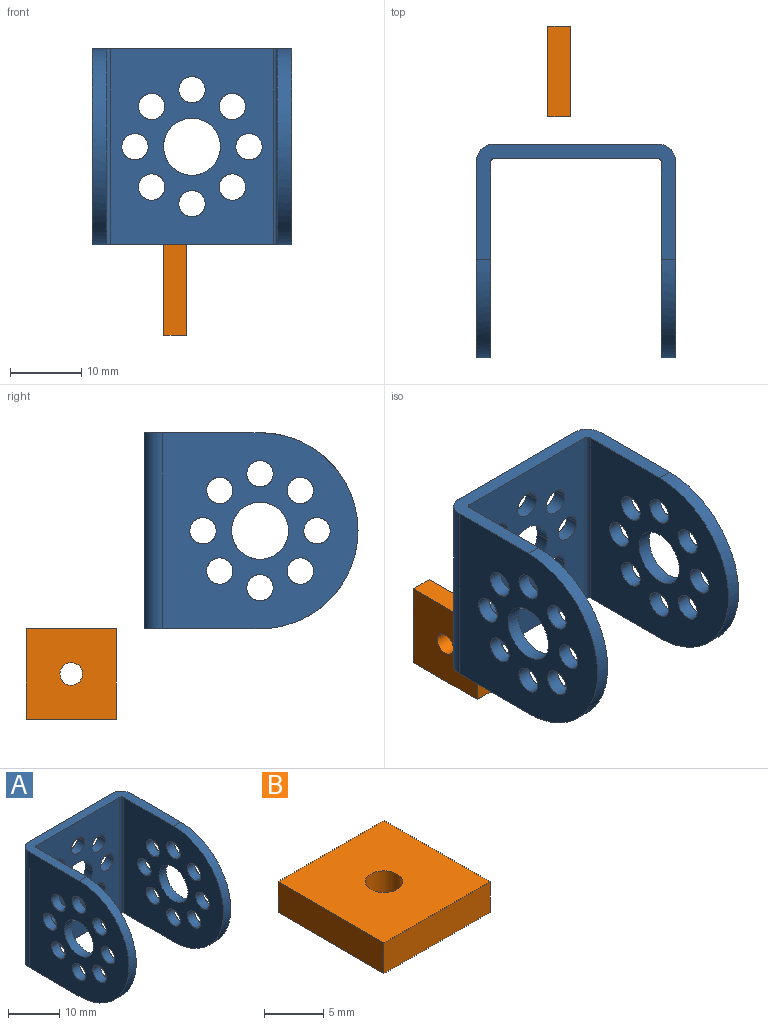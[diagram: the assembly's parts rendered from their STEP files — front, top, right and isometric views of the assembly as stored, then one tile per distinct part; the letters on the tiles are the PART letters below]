
ASSEMBLY  parts=2 mates=2
PART A: 68 faces, bbox 28x30x27.5 mm
  f0: cylinder r=1.85mm len=3.7mm, axis (1,0,0), area 11.6mm2, adj f1,f38,f40
  f1: cylinder r=1.85mm len=3.7mm, axis (1,0,0), area 11.6mm2, adj f0,f38,f40
  f2: cylinder r=1.85mm len=3.7mm, axis (1,0,0), area 11.6mm2, adj f3,f38,f40
  f3: cylinder r=1.85mm len=3.7mm, axis (1,0,0), area 11.6mm2, adj f2,f38,f40
  f4: cylinder r=1.85mm len=3.7mm, axis (1,0,0), area 11.6mm2, adj f5,f38,f40
  f5: cylinder r=1.85mm len=3.7mm, axis (1,0,0), area 11.6mm2, adj f4,f38,f40
  f6: cylinder r=1.85mm len=3.7mm, axis (1,0,0), area 11.6mm2, adj f7,f38,f40
  f7: cylinder r=1.85mm len=3.7mm, axis (1,0,0), area 11.6mm2, adj f6,f38,f40
  f8: cylinder r=1.85mm len=3.7mm, axis (1,0,0), area 11.6mm2, adj f9,f38,f40
  f9: cylinder r=1.85mm len=3.7mm, axis (1,0,0), area 11.6mm2, adj f8,f38,f40
  f10: cylinder r=1.85mm len=3.7mm, axis (1,0,0), area 11.6mm2, adj f11,f38,f40
  f11: cylinder r=1.85mm len=3.7mm, axis (1,0,0), area 11.6mm2, adj f10,f38,f40
  f12: cylinder r=1.85mm len=3.7mm, axis (1,0,0), area 11.6mm2, adj f13,f38,f40
  f13: cylinder r=1.85mm len=3.7mm, axis (1,0,0), area 11.6mm2, adj f12,f38,f40
  f14: cylinder r=4mm len=8mm, axis (1,0,0), area 25.1mm2, adj f15,f38,f40
  f15: cylinder r=4mm len=8mm, axis (1,0,0), area 25.1mm2, adj f14,f38,f40
  f16: cylinder r=1.85mm len=3.7mm, axis (1,0,0), area 11.6mm2, adj f17,f38,f40
  f17: cylinder r=1.85mm len=3.7mm, axis (1,0,0), area 11.6mm2, adj f16,f38,f40
  f18: cylinder r=1.85mm len=3.7mm, axis (0,1,0), area 11.6mm2, adj f19,f36,f42
  f19: cylinder r=1.85mm len=3.7mm, axis (0,1,0), area 11.6mm2, adj f18,f36,f42
  f20: cylinder r=1.85mm len=3.7mm, axis (0,1,0), area 11.6mm2, adj f21,f36,f42
  f21: cylinder r=1.85mm len=3.7mm, axis (0,1,0), area 11.6mm2, adj f20,f36,f42
  f22: cylinder r=1.85mm len=3.7mm, axis (0,1,0), area 11.6mm2, adj f23,f36,f42
  f23: cylinder r=1.85mm len=3.7mm, axis (0,1,0), area 11.6mm2, adj f22,f36,f42
  f24: cylinder r=1.85mm len=3.7mm, axis (0,1,0), area 11.6mm2, adj f25,f36,f42
  f25: cylinder r=1.85mm len=3.7mm, axis (0,1,0), area 11.6mm2, adj f24,f36,f42
  f26: cylinder r=1.85mm len=3.7mm, axis (0,1,0), area 11.6mm2, adj f27,f36,f42
  f27: cylinder r=1.85mm len=3.7mm, axis (0,1,0), area 11.6mm2, adj f26,f36,f42
  f28: cylinder r=1.85mm len=3.7mm, axis (0,1,0), area 11.6mm2, adj f29,f36,f42
  f29: cylinder r=1.85mm len=3.7mm, axis (0,1,0), area 11.6mm2, adj f28,f36,f42
  f30: cylinder r=1.85mm len=3.7mm, axis (0,1,0), area 11.6mm2, adj f31,f36,f42
  f31: cylinder r=1.85mm len=3.7mm, axis (0,1,0), area 11.6mm2, adj f30,f36,f42
  f32: cylinder r=1.85mm len=3.7mm, axis (0,1,0), area 11.6mm2, adj f33,f36,f42
  f33: cylinder r=1.85mm len=3.7mm, axis (0,1,0), area 11.6mm2, adj f32,f36,f42
  f34: cylinder r=4mm len=8mm, axis (0,1,0), area 25.1mm2, adj f35,f36,f42
  f35: cylinder r=4mm len=8mm, axis (0,1,0), area 25.1mm2, adj f34,f36,f42
  f36: plane 27.5x22.98mm, normal (0,-1,0), area 495.8mm2, adj f18,f19,f20,f21,f22,f23,f24,f25
  f37: cylinder r=0.51mm len=27.5mm, axis (0,0,-1), area 21.9mm2, adj f36,f38,f46,f48
  f38: plane 27.5x27.49mm, normal (-1,0,0), area 538.6mm2, adj f0,f1,f2,f3,f4,f5,f6,f7
  f39: cylinder r=13.75mm len=27.5mm, axis (1,0,0), area 86.4mm2, adj f38,f40,f46,f48
  f40: plane 27.5x27.49mm, normal (1,0,0), area 538.6mm2, adj f0,f1,f2,f3,f4,f5,f6,f7
  f41: cylinder r=2.51mm len=27.5mm, axis (0,0,-1), area 108.3mm2, adj f40,f42,f46,f48
  f42: plane 27.5x22.98mm, normal (0,1,0), area 495.8mm2, adj f18,f19,f20,f21,f22,f23,f24,f25
  f43: cylinder r=2.51mm len=27.5mm, axis (0,0,-1), area 108.3mm2, adj f42,f44,f46,f48
  f44: plane 27.5x27.49mm, normal (-1,0,0), area 538.6mm2, adj f43,f45,f46,f48,f49,f50,f51,f52
  f45: cylinder r=13.75mm len=27.5mm, axis (1,0,0), area 86.4mm2, adj f44,f46,f48,f67
  f46: plane 28x16.25mm, normal (0,0,1), area 110.4mm2, adj f36,f37,f38,f39,f40,f41,f42,f43
  f47: cylinder r=0.51mm len=27.5mm, axis (0,0,-1), area 21.9mm2, adj f36,f46,f48,f67
  f48: plane 28x16.25mm, normal (0,0,-1), area 110.4mm2, adj f36,f37,f38,f39,f40,f41,f42,f43
  f49: cylinder r=1.85mm len=3.7mm, axis (1,0,0), area 11.6mm2, adj f44,f50,f67
  f50: cylinder r=1.85mm len=3.7mm, axis (1,0,0), area 11.6mm2, adj f44,f49,f67
  f51: cylinder r=1.85mm len=3.7mm, axis (1,0,0), area 11.6mm2, adj f44,f52,f67
  f52: cylinder r=1.85mm len=3.7mm, axis (1,0,0), area 11.6mm2, adj f44,f51,f67
  f53: cylinder r=1.85mm len=3.7mm, axis (1,0,0), area 11.6mm2, adj f44,f54,f67
  f54: cylinder r=1.85mm len=3.7mm, axis (1,0,0), area 11.6mm2, adj f44,f53,f67
  f55: cylinder r=1.85mm len=3.7mm, axis (1,0,0), area 11.6mm2, adj f44,f56,f67
  f56: cylinder r=1.85mm len=3.7mm, axis (1,0,0), area 11.6mm2, adj f44,f55,f67
  f57: cylinder r=1.85mm len=3.7mm, axis (1,0,0), area 11.6mm2, adj f44,f58,f67
  f58: cylinder r=1.85mm len=3.7mm, axis (1,0,0), area 11.6mm2, adj f44,f57,f67
  f59: cylinder r=1.85mm len=3.7mm, axis (1,0,0), area 11.6mm2, adj f44,f60,f67
  f60: cylinder r=1.85mm len=3.7mm, axis (1,0,0), area 11.6mm2, adj f44,f59,f67
  f61: cylinder r=1.85mm len=3.7mm, axis (1,0,0), area 11.6mm2, adj f44,f62,f67
  f62: cylinder r=1.85mm len=3.7mm, axis (1,0,0), area 11.6mm2, adj f44,f61,f67
  f63: cylinder r=4mm len=8mm, axis (1,0,0), area 25.1mm2, adj f44,f64,f67
  f64: cylinder r=4mm len=8mm, axis (1,0,0), area 25.1mm2, adj f44,f63,f67
  f65: cylinder r=1.85mm len=3.7mm, axis (1,0,0), area 11.6mm2, adj f44,f66,f67
  f66: cylinder r=1.85mm len=3.7mm, axis (1,0,0), area 11.6mm2, adj f44,f65,f67
  f67: plane 27.52x27.5mm, normal (1,0,0), area 538.6mm2, adj f45,f46,f47,f48,f49,f50,f51,f52
PART B: 7 faces, bbox 12.7x12.7x3.2 mm
  f0: plane 12.7x3.18mm, normal (-1,0,0), area 40.3mm2, adj f1,f3,f5,f6
  f1: plane 12.7x3.18mm, normal (0,-1,0), area 40.3mm2, adj f0,f2,f5,f6
  f2: plane 12.7x3.18mm, normal (1,0,0), area 40.3mm2, adj f1,f3,f5,f6
  f3: plane 12.7x3.18mm, normal (0,1,0), area 40.3mm2, adj f0,f2,f5,f6
  f4: cylinder r=1.59mm len=3.18mm, axis (0,0,-1), area 31.7mm2, adj f5,f6
  f5: plane 12.7x12.7mm, normal (0,0,1), area 153.4mm2, adj f0,f1,f2,f3,f4
  f6: plane 12.7x12.7mm, normal (0,0,-1), area 153.4mm2, adj f0,f1,f2,f3,f4
PLACE A t=(0.16,-19.23,27.59)mm
PLACE B rot(axis=(0.58,0.58,0.58),120deg) t=(-3.79,-8.97,7.49)mm
MATE parallel B.f3 <-> A.f48  axis (0,0,1) through (-3.79,-15.32,13.84)mm
MATE planar B.f3 <-> A.f48  axis (0,0,1) through (-2.21,-2.62,13.84)mm
